SOLIDWORKS PART (.sldprt)
format: sldprt  version: not decoded by parser v0  size: 186,880 bytes
history: native  units: mm
features: plane x3, sketch x3, extrude x2, chamfer x2, material x1, cut_extrude x1 (+8 scaffold rows collapsed)
feature tree (20):
  scaffold x8  (default folders/planes/origin — collapsed)
  material  "Material <not specified>"
  plane  "Alzado"
  plane  "Planta"
  plane  "Vista lateral"
  sketch  "Croquis1"  dims[D1=17.0mm D2=4.0mm D3=2.0mm D4=8.5mm]
  extrude  "Extruir1"  Depth=8.4mm
  sketch  "Croquis2"  dims[D1=1.7mm D2=2.0mm D3=1.0mm D4=0.8mm D5=0.8mm]
  cut_extrude  "Cortar-Extruir1"  Depth=5.4mm
  chamfer  "Chaflán1"  Distance=0.6mm Angle=45deg
  sketch  "Croquis3"  dims[D1=10.0mm D2=2.3mm D3=1.3mm D4=1.3mm D5=3.5mm D6=0.85mm]
  extrude  "Extruir2"  Depth=5.4mm
  chamfer  "Chaflán2"  Distance=0.3mm Angle=45deg PW2_UID_val=0mm
decode coverage: 8 of 8 modeling features carry decoded parameters
note: suppression state not decoded; provenance and decode notes live in map.json
